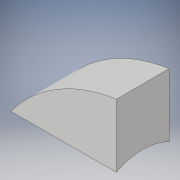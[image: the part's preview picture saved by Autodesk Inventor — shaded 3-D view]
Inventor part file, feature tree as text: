
AUTODESK INVENTOR PART (.ipt)
format: ipt  version: 2019 (Build 230136000, 136)  size: 104,448 bytes
history: native  units: mm
features: extrude x2, sketch x2
ambient origin geometry x8: Origin, YZ Plane, XZ Plane, XY Plane, X Axis, Y Axis, Z Axis, Center Point
bodies: Solid1 (feature_tree)
feature tree (4):
  extrude  "Extrusion1"  Depth=30.0mm
  extrude  "Extrusion2"  Depth=26.8mm
  sketch  "Sketch1"  dims[d0=53.6mm d3=30.0mm]
  sketch  "Sketch2"  dims[d4=25.0mm d5=26.8mm d6=50.0mm d7=0.0mm d8=25.0mm d9=0.0mm]
